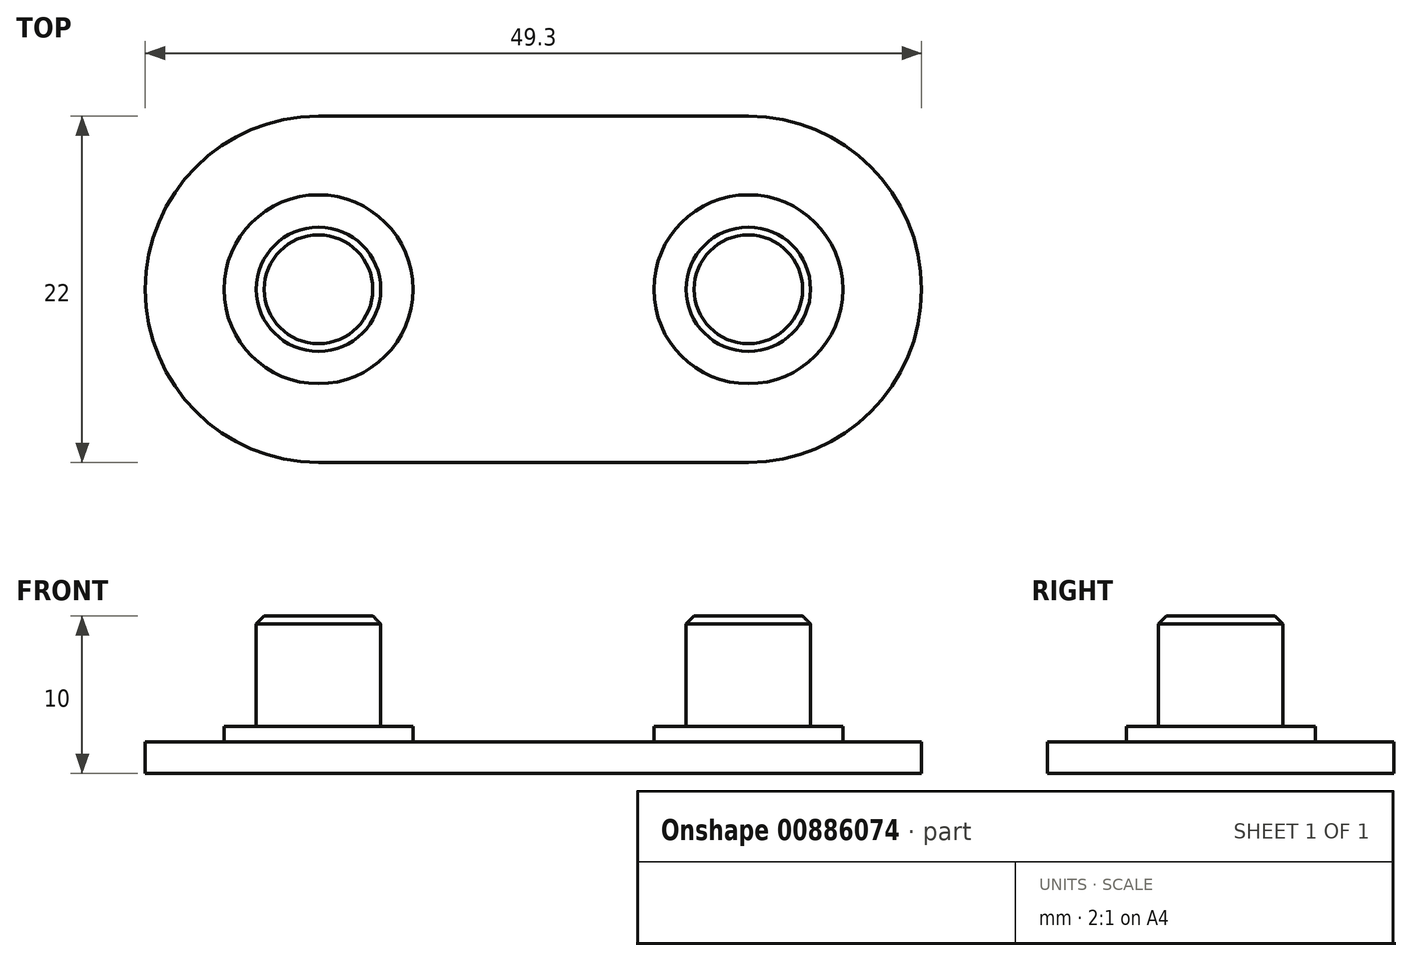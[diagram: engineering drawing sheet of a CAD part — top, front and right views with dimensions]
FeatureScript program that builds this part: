
annotation { "Feature Type Name" : "Feature", "Feature Type Description" : "" }
export const myFeature = defineFeature(function(context is Context, id is Id, definition is map)
    precondition{}
    {
        {
            var Q0;
            Q0=qCreatedBy(makeId("Top.planeOp"),FACE);
            var sketch = newSketch(context, id + "F0", { "sketchPlane" : qUnion([Q0])});
            skCircle(sketch, "E0", {"center": v(-13.65, 0) * mm, "radius": 11.15 * mm});
            skCircle(sketch, "E1", {"center": v(13.65, 0) * mm, "radius": 11.15 * mm});
            skCircle(sketch, "E2", {"center": v(13.65, 0) * mm, "radius": 13.15 * mm});
            skCircle(sketch, "E3", {"center": v(-13.65, 0) * mm, "radius": 13.15 * mm});
            skLineSegment(sketch, "E4", {"start": v(-13.65, 0) * mm, "end": v(13.65, 0) * mm, "construction": true});
            skPoint(sketch, "E5", {"position": v(-0.5, 0) * mm});
            skPoint(sketch, "E6", {"position": v(0.5, 0) * mm});
            skSolve(sketch);
        }
        {
            var Q0;
            Q0=qCreatedBy(makeId("Top.planeOp"),FACE);
            var sketch = newSketch(context, id + "F1", { "sketchPlane" : qUnion([Q0])});
            skCircle(sketch, "E7", {"center": v(-13.65, 0) * mm, "radius": 3.95 * mm});
            skCircle(sketch, "E8", {"center": v(13.65, 0) * mm, "radius": 3.95 * mm});
            skSolve(sketch);
        }
        {
            var Q0;
            Q0 = qSketchRegion(id + "F1", true);
            extrude(context, id + "F2", {"entities" : qUnion([Q0]), "depth" : 7 * mm, "offsetDistance" : 25 * mm});
        }
        {
            var Q0;
            Q0=makeQuery(id+"F2.opExtrude","CAP_FACE",FACE,{"disambiguationData":[OSD([sQuery(id+"F1.wireOp",EDGE,"E8")])],"isStart":true});
            var sketch = newSketch(context, id + "F3", { "sketchPlane" : qUnion([Q0])});
            skCircle(sketch, "E9", {"center": v(13.65, 0) * mm, "radius": 6 * mm});
            skCircle(sketch, "E10", {"center": v(-13.65, 0) * mm, "radius": 6 * mm});
            skSolve(sketch);
        }
        {
            var Q0;
            Q0 = qSketchRegion(id + "F3", true);
            extrude(context, id + "F4", {"entities" : qUnion([Q0]), "operationType" : NewBodyOperationType.ADD, "depth" : 1 * mm, "offsetDistance" : 25 * mm});
        }
        {
            var Q0;
            Q0=makeQuery(id+"F4.opExtrude","CAP_FACE",FACE,{"disambiguationData":[OSD([sQuery(id+"F3.wireOp",EDGE,"E9")])],"isStart":false});
            var sketch = newSketch(context, id + "F5", { "sketchPlane" : qUnion([Q0])});
            skLineSegment(sketch, "E11.bottom", {"start": v(-13.65, -11) * mm, "end": v(13.65, -11) * mm});
            skLineSegment(sketch, "E11.top", {"start": v(-13.65, 11) * mm, "end": v(13.65, 11) * mm});
            skLineSegment(sketch, "E11.left", {"start": v(-13.65, -11) * mm, "end": v(-13.65, 11) * mm, "construction": true});
            skLineSegment(sketch, "E11.right", {"start": v(13.65, -11) * mm, "end": v(13.65, 11) * mm, "construction": true});
            skPoint(sketch, "E11.middle", {"position": v(0, 0) * mm});
            skArc(sketch, "E12", {"start": v(13.65, -11) * mm, "mid": v(24.65, 0) * mm, "end": v(13.65, 11) * mm});
            skArc(sketch, "E13", {"start": v(-13.65, 11) * mm, "mid": v(-24.65, 0) * mm, "end": v(-13.65, -11) * mm});
            skSolve(sketch);
        }
        {
            var Q0;
            Q0 = qSketchRegion(id + "F5", true);
            extrude(context, id + "F6", {"entities" : qUnion([Q0]), "operationType" : NewBodyOperationType.ADD, "depth" : 2 * mm, "offsetDistance" : 25 * mm});
        }
        {
            var Q0;
            Q0=makeQuery(id+"F2.opExtrude","CAP_EDGE",EDGE,{"disambiguationData":[OSD([sQuery(id+"F1.wireOp",EDGE,"E7")])],"isStart":false});
            var Q1;
            Q1=makeQuery(id+"F2.opExtrude","CAP_EDGE",EDGE,{"disambiguationData":[OSD([sQuery(id+"F1.wireOp",EDGE,"E8")])],"isStart":false});
            chamfer(context, id + "F7", {"entities" : qUnion([Q0, Q1]), "width" : .5 * mm, "tangentPropagation" : true});
        }
    });
